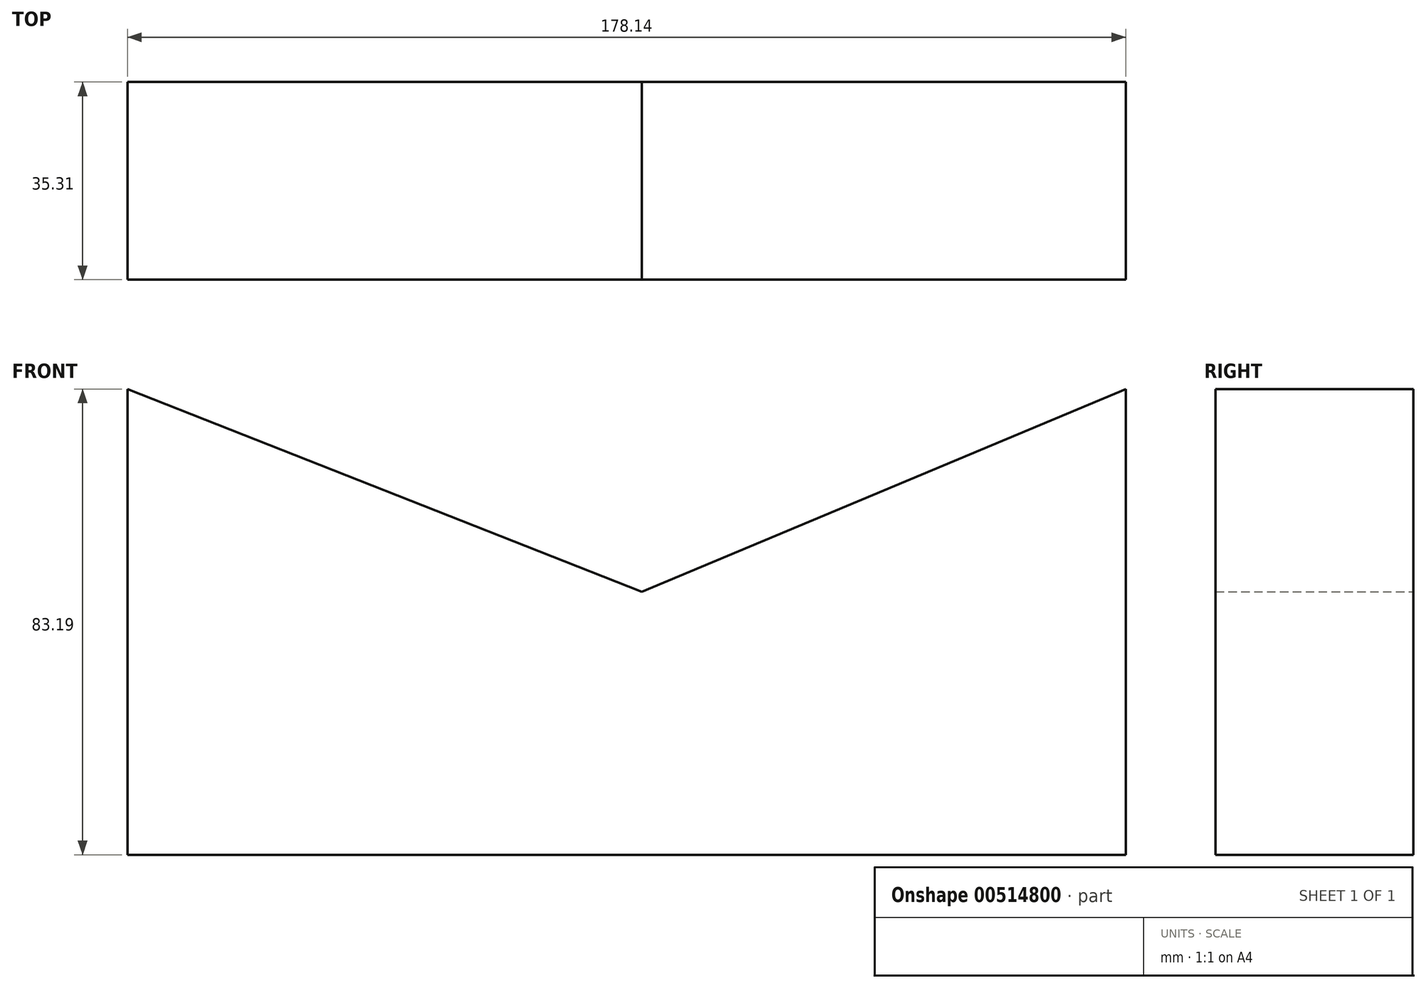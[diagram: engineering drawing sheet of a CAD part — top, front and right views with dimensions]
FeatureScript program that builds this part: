
annotation { "Feature Type Name" : "Feature", "Feature Type Description" : "" }
export const myFeature = defineFeature(function(context is Context, id is Id, definition is map)
    precondition{}
    {
        {
            var Q0;
            Q0=qCreatedBy(makeId("Front.planeOp"),FACE);
            var sketch = newSketch(context, id + "F0", { "sketchPlane" : qUnion([Q0])});
            skLineSegment(sketch, "E0.top", {"start": v(-73.35, -76.84) * mm, "end": v(104.79, -76.84) * mm});
            skLineSegment(sketch, "E0.left", {"start": v(-73.35, 6.35) * mm, "end": v(-73.35, -76.84) * mm});
            skLineSegment(sketch, "E0.right", {"start": v(104.79, 6.35) * mm, "end": v(104.79, -76.84) * mm});
            skLineSegment(sketch, "E1", {"start": v(-73.35, 6.35) * mm, "end": v(18.42, -29.85) * mm});
            skLineSegment(sketch, "E2", {"start": v(18.42, -29.85) * mm, "end": v(104.79, 6.35) * mm});
            skSolve(sketch);
        }
        {
            var Q0;
            Q0 = qSketchRegion(id + "F0", true);
            extrude(context, id + "F1", {"entities" : qUnion([Q0]), "depth" : 35.3 * mm, "offsetDistance" : 25.4 * mm});
        }
    });
